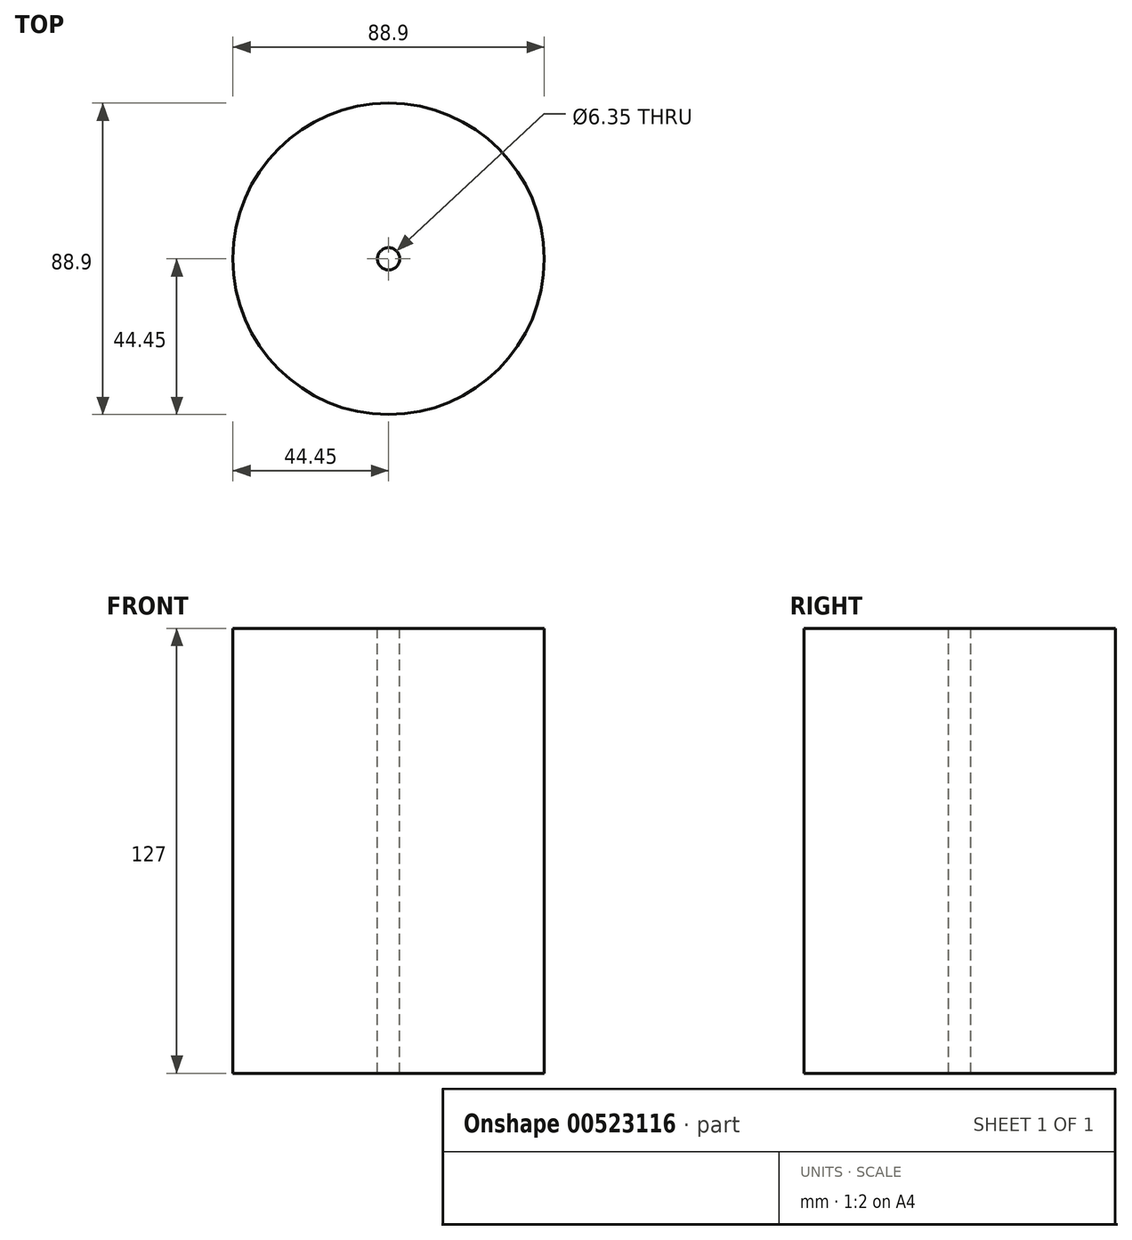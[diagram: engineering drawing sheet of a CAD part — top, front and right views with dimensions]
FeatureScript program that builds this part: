
annotation { "Feature Type Name" : "Feature", "Feature Type Description" : "" }
export const myFeature = defineFeature(function(context is Context, id is Id, definition is map)
    precondition{}
    {
        {
            var Q0;
            Q0=qCreatedBy(makeId("Top.planeOp"),FACE);
            var sketch = newSketch(context, id + "F0", { "sketchPlane" : qUnion([Q0])});
            skCircle(sketch, "E0", {"center": v(0, 0) * mm, "radius": 44.45 * mm});
            skSolve(sketch);
        }
        {
            var Q0;
            Q0=makeQuery(id+"F0.imprint","IMPRINT",FACE,{"disambiguationData":[TD([[makeQuery(id+"F0.imprint","IMPRINT",EDGE,{"derivedFrom":sQuery(id+"F0.wireOp",EDGE,"E0")}),1.0]])]});
            extrude(context, id + "F1", {"entities" : qUnion([Q0]), "depth" : 127 * mm, "offsetDistance" : 25.4 * mm});
        }
        {
            var Q0;
            Q0=makeQuery(id+"F1.opExtrude","CAP_FACE",FACE,{"disambiguationData":[OSD([sQuery(id+"F0.wireOp",EDGE,"E0")])],"isStart":false});
            var sketch = newSketch(context, id + "F2", { "sketchPlane" : qUnion([Q0])});
            skCircle(sketch, "E1", {"center": v(0, 0) * mm, "radius": 3.18 * mm});
            skSolve(sketch);
        }
        {
            var Q0;
            Q0=makeQuery(id+"F2.imprint","IMPRINT",FACE,{"disambiguationData":[TD([[makeQuery(id+"F2.imprint","IMPRINT",EDGE,{"derivedFrom":sQuery(id+"F2.wireOp",EDGE,"E1")}),1.0]])]});
            extrude(context, id + "F3", {"entities" : qUnion([Q0]), "operationType" : NewBodyOperationType.REMOVE, "endBound" : BoundingType.THROUGH_ALL, "oppositeDirection" : true, "depth" : 25.4 * mm, "offsetDistance" : 25.4 * mm});
        }
    });
